# Revit family: Family-EB60MSB1-EB60MSG1
name_source: partatom
category: Generic Models
units: mm (PartAtom-declared; Revit-internal decimal feet)

## family parameters
Always vertical = Yes
Can host rebar = No
Cut with Voids When Loaded = No
Part Type = Normal
Room Calculation Point = No
Round Connector Dimension = Use Diameter
Shared = No
Work Plane-Based = No

## types (2) — shared parameters
Cavity - minimum depth = 545 mm  [stored 1.78806 ft]
Cavity - minimum height = 450 mm  [stored 1.47638 ft]
Cavity - minimum width = 560 mm  [stored 1.83727 ft]
Chassis - Depth = 460 mm  [stored 1.50919 ft]
Chassis - Height = 445 mm  [stored 1.45997 ft]
Chassis - width = 560 mm  [stored 1.83727 ft]
Connector Note = 220-240 V, 50Hz, 20 A
Description = Built-in Coffee Maker, 30cm
Manufacturer = Fisher & Paykel Appliances
Material - Chassis = Fisher & Paykel - Aluminium
Product - Overall depth = 480 mm  [stored 1.5748 ft]
Product - Overall height = 458 mm
Product - Overall width = 596 mm  [stored 1.95538 ft]
Product - width = 596 mm  [stored 1.95538 ft]
URL = www.fisherpaykel.com
zero-valued in all types: Default Elevation

## per-type parameters (varying)
| type | Material - Glass |
| EB60MSB1 | Fisher & Paykel - Glass, Black |
| EB60MSG1 | Fisher & Paykel - Glass, Grey |

note: column(s) folded — value = type name in every type: Model

note: [stored X ft] marks values corroborated as IEEE doubles in the binary element streams (Revit-internal decimal feet)

## geometry (parser evidence)
native form markers: Sweep x1
no freeform markers — native parametric forms only
